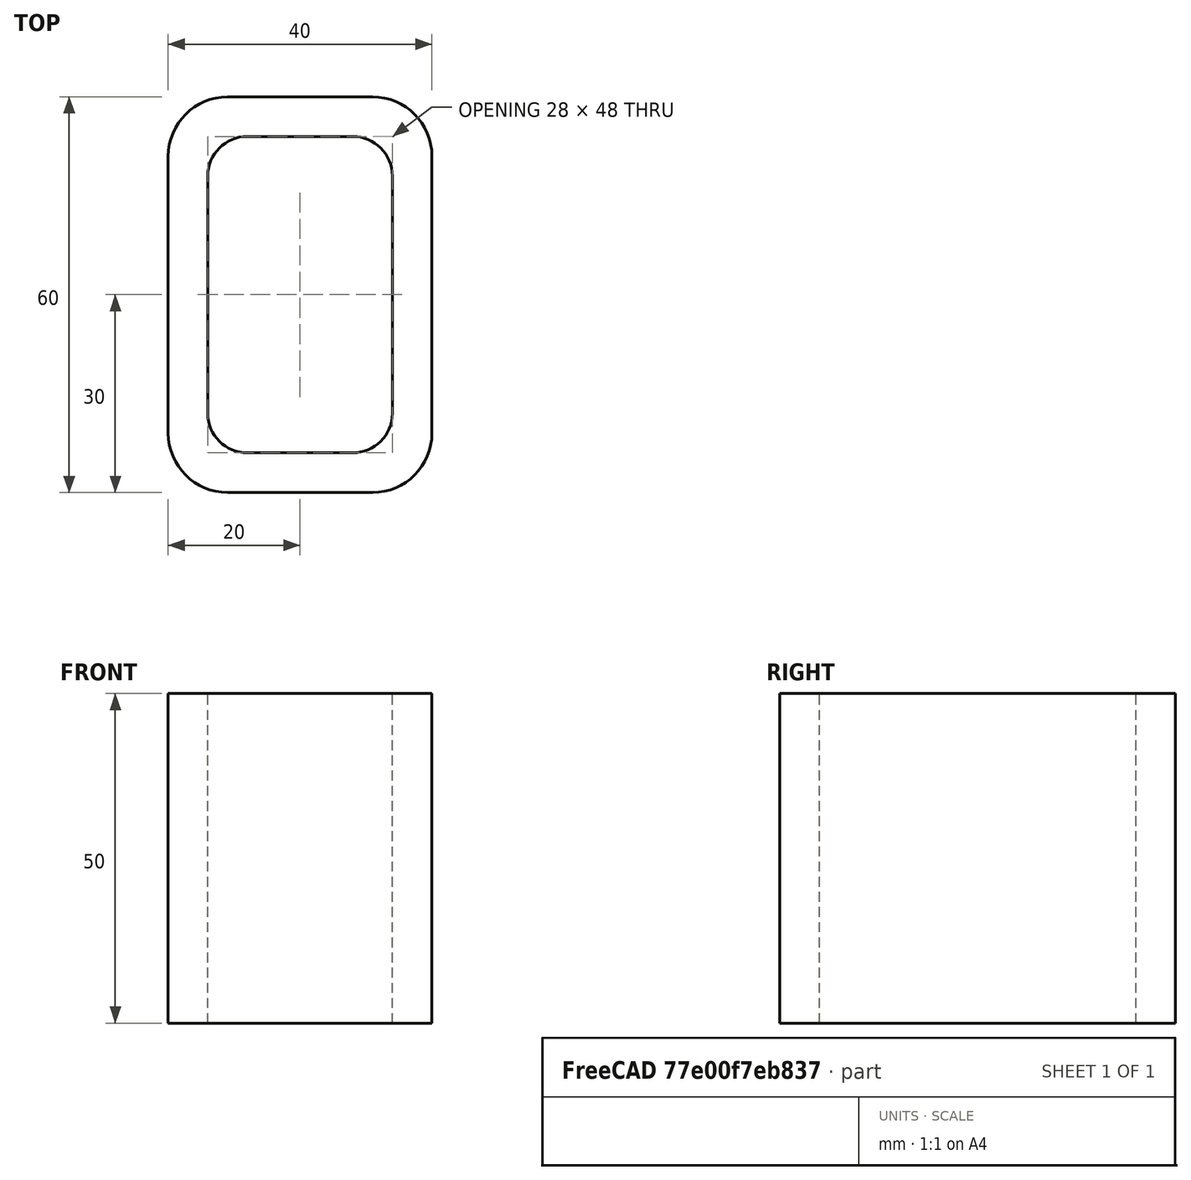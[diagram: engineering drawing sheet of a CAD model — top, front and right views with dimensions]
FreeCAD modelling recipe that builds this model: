
FCSTD DOCUMENT  (FreeCAD 0.15R4671 (Git))
Label: Rectangular hollow section 60x40x6 EN10219 S235JRH
License: All rights reserved
LicenseURL: http://en.wikipedia.org/wiki/All_rights_reserved
objects: Sketcher::SketchObject×1, Part::Extrusion×1
note: 2 computed .brp shape members not serialized (recipe doc carries the construction recipe); baked Part::Feature solids carry a one-line shape summary decoded from their .brp

FEATURE [Sketcher::SketchObject] Sketch
  sketch-geometry (16):
    g0: LineSegment StartX=-8 StartY=24 StartZ=0 EndX=8 EndY=24 EndZ=0
    g1: LineSegment StartX=14 StartY=18 StartZ=0 EndX=14 EndY=-18 EndZ=0
    g2: LineSegment StartX=8 StartY=-24 StartZ=0 EndX=-8 EndY=-24 EndZ=0
    g3: LineSegment StartX=-14 StartY=-18 StartZ=0 EndX=-14 EndY=18 EndZ=0
    g4: LineSegment StartX=-11 StartY=30 StartZ=0 EndX=11 EndY=30 EndZ=0
    g5: LineSegment StartX=20 StartY=21 StartZ=0 EndX=20 EndY=-21 EndZ=0
    g6: LineSegment StartX=11 StartY=-30 StartZ=0 EndX=-11 EndY=-30 EndZ=0
    g7: LineSegment StartX=-20 StartY=-21 StartZ=0 EndX=-20 EndY=21 EndZ=0
    g8: ArcOfCircle CenterX=-8 CenterY=18 CenterZ=0 NormalX=0 NormalY=0 NormalZ=1 Radius=6 StartAngle=1.5708 EndAngle=3.14159
    g9: ArcOfCircle CenterX=8 CenterY=18 CenterZ=0 NormalX=0 NormalY=0 NormalZ=1 Radius=6 StartAngle=0 EndAngle=1.5708
    g10: ArcOfCircle CenterX=8 CenterY=-18 CenterZ=0 NormalX=0 NormalY=0 NormalZ=1 Radius=6 StartAngle=4.71239 EndAngle=6.28319
    g11: ArcOfCircle CenterX=-8 CenterY=-18 CenterZ=0 NormalX=0 NormalY=0 NormalZ=1 Radius=6 StartAngle=3.14159 EndAngle=4.71239
    g12: ArcOfCircle CenterX=11 CenterY=21 CenterZ=0 NormalX=0 NormalY=0 NormalZ=1 Radius=9 StartAngle=0 EndAngle=1.5708
    g13: ArcOfCircle CenterX=11 CenterY=-21 CenterZ=0 NormalX=0 NormalY=0 NormalZ=1 Radius=9 StartAngle=4.71239 EndAngle=6.28319
    g14: ArcOfCircle CenterX=-11 CenterY=-21 CenterZ=0 NormalX=0 NormalY=0 NormalZ=1 Radius=9 StartAngle=3.14159 EndAngle=4.71239
    g15: ArcOfCircle CenterX=-11 CenterY=21 CenterZ=0 NormalX=0 NormalY=0 NormalZ=1 Radius=9 StartAngle=1.5708 EndAngle=3.14159
  constraints (36):
    c: Horizontal(g2)
    c: Vertical(g3)
    c: Horizontal(g6)
    c: Vertical(g7)
    c: Tangent(g3,g8) = 1.5708
    c: Tangent(g0,g8) = 1.5708
    c: Tangent(g0,g9) = 1.5708
    c: Tangent(g1,g9) = 1.5708
    c: Tangent(g1,g10) = 1.5708
    c: Tangent(g2,g10) = 1.5708
    c: Tangent(g2,g11) = 1.5708
    c: Tangent(g3,g11) = 1.5708
    c: Tangent(g4,g12) = 1.5708
    c: Tangent(g5,g12) = 1.5708
    c: Tangent(g5,g13) = 1.5708
    c: Tangent(g6,g13) = 1.5708
    c: Tangent(g6,g14) = 1.5708
    c: Tangent(g7,g14) = 1.5708
    c: Tangent(g7,g15) = 1.5708
    c: Tangent(g4,g15) = 1.5708
    c: Equal(g9,g8)
    c: Equal(g9,g11)
    c: Equal(g9,g10)
    c: Equal(g12,g15)
    c: Equal(g12,g14)
    c: Equal(g12,g13)
    c: Symmetric(g4,g6,g-1)
    c: Symmetric(g7,g5,g-2)
    c: DistanceY(g4,g6) = -60
    c: DistanceX(g7,g5) = 40
    c: Symmetric(g3,g1,g-2)
    c: Symmetric(g0,g2,g-1)
    c: DistanceY(g0,g4) = 6
    c: DistanceX(g5,g1) = -6
    c: Radius(g9) = 6
    c: Radius(g12) = 9
FEATURE [Part::Extrusion] Extrude  label="Rectangular hollow section 60x40x6 EN10219 S235JRH"
  Base = -> Sketch
  Dir = (0,0,50)
  Solid = true
